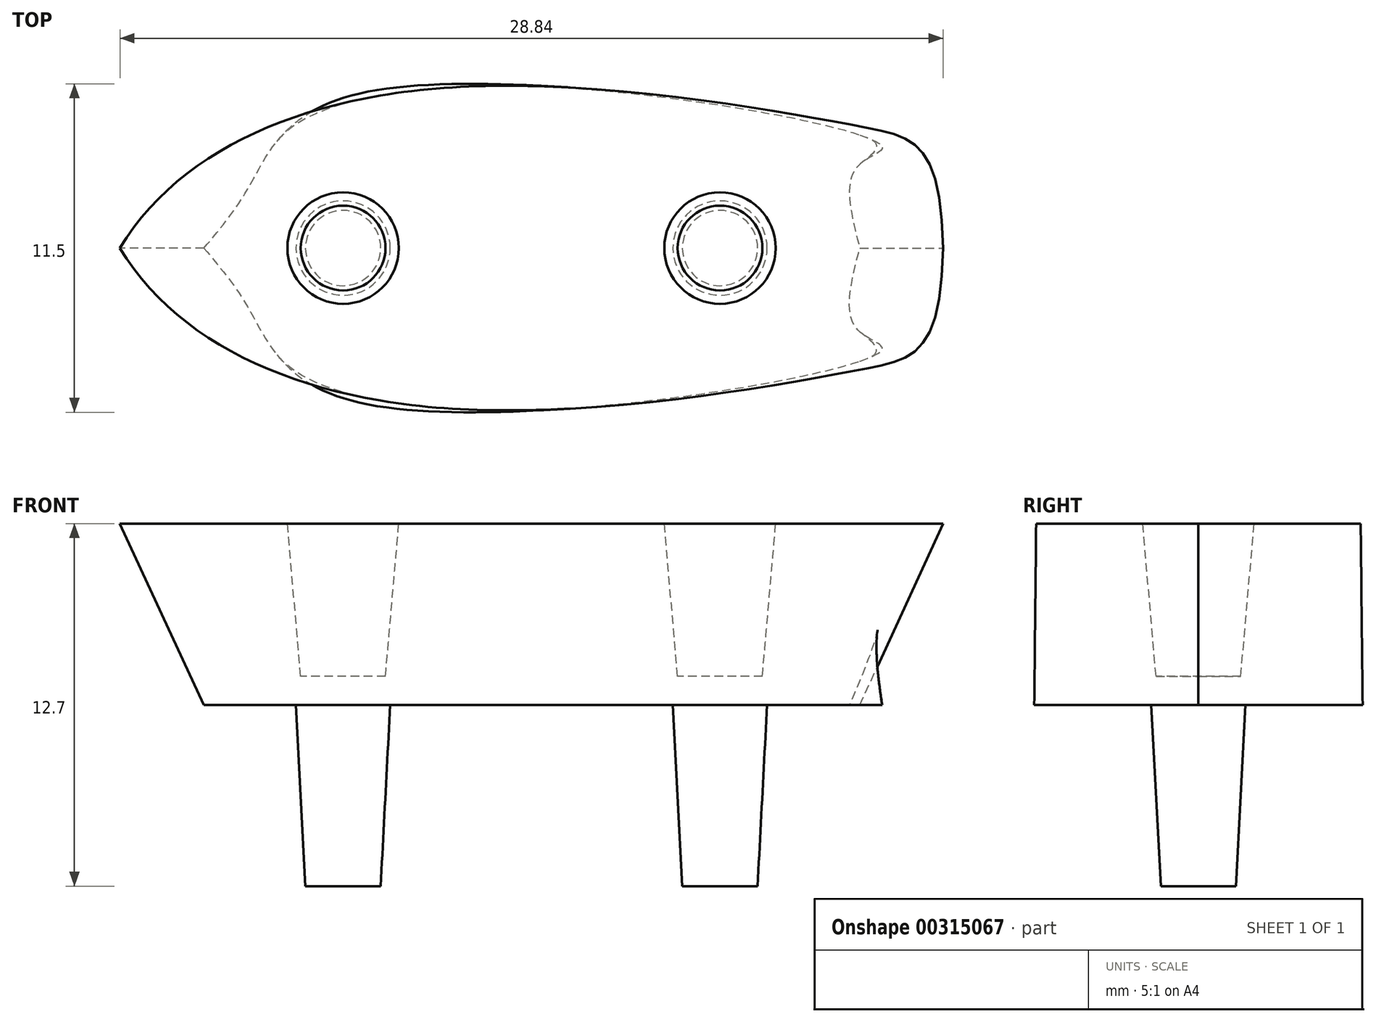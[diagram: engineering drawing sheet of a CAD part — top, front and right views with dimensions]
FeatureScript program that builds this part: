
annotation { "Feature Type Name" : "Feature", "Feature Type Description" : "" }
export const myFeature = defineFeature(function(context is Context, id is Id, definition is map)
    precondition{}
    {
        {
            var Q0;
            Q0=qCreatedBy(makeId("Top.planeOp"),FACE);
            var sketch = newSketch(context, id + "F0", { "sketchPlane" : qUnion([Q0])});
            skCircle(sketch, "E0", {"center": v(-6.6, 0) * mm, "radius": 1.65 * mm});
            skCircle(sketch, "E1", {"center": v(6.6, 0) * mm, "radius": 1.65 * mm});
            skFitSpline(sketch, "E2", {"points": [v(-14.42, 0) * mm, v(-3.67, 5.56) * mm, v(11.5, 4.26) * mm, v(14.42, 0) * mm], "startDerivative": vector(16.36, 27.23) * mm, "endDerivative": vector(1.16, -47.54) * mm});
            skFitSpline(sketch, "E3.MirrorCS", {"points": [v(-14.42, 0) * mm, v(-3.67, -5.56) * mm, v(11.5, -4.26) * mm, v(14.42, 0) * mm], "startDerivative": vector(16.36, -27.23) * mm, "endDerivative": vector(1.16, 47.54) * mm});
            skFitSpline(sketch, "E4", {"points": [v(-11.48, 0) * mm, v(-4.9, 4.04) * mm, v(10.6, 3.36) * mm, v(11.48, 0) * mm], "startDerivative": vector(14.55, 19.73) * mm, "endDerivative": vector(1.2, -39.33) * mm});
            skFitSpline(sketch, "E5.MirrorCS", {"points": [v(-11.48, 0) * mm, v(-4.9, -4.04) * mm, v(10.6, -3.36) * mm, v(11.48, 0) * mm], "startDerivative": vector(14.55, -19.73) * mm, "endDerivative": vector(1.2, 39.33) * mm});
            skCircle(sketch, "E6.0", {"center": v(-6.6, 0) * mm, "radius": 1.4 * mm});
            skCircle(sketch, "E7.0", {"center": v(6.6, 0) * mm, "radius": 1.4 * mm});
            skSolve(sketch);
        }
        {
            var Q0;
            Q0=qCreatedBy(makeId("Top.planeOp"),FACE);
            cPlane(context, id + "F1", {"entities" : qUnion([Q0]), "cplaneType" : CPlaneType.OFFSET, "offset" : 6.35 * mm, "width" : 152.4 * mm, "height" : 152.4 * mm});
        }
        {
            var Q0;
            Q0=qCreatedBy(id+"F1.planeOp",FACE);
            var sketch = newSketch(context, id + "F2", { "sketchPlane" : qUnion([Q0])});
            skFitSpline(sketch, "E8", {"points": [v(-14.42, 0) * mm, v(-3.67, 5.56) * mm, v(11.5, 4.26) * mm, v(14.42, 0) * mm], "startDerivative": vector(16.36, 27.23) * mm, "endDerivative": vector(1.16, -47.54) * mm});
            skFitSpline(sketch, "E9.MirrorCS", {"points": [v(-14.42, 0) * mm, v(-3.67, -5.56) * mm, v(11.5, -4.26) * mm, v(14.42, 0) * mm], "startDerivative": vector(16.36, -27.23) * mm, "endDerivative": vector(1.16, 47.54) * mm});
            skSolve(sketch);
        }
        {
            var Q0;
            Q0=qCreatedBy(makeId("Top.planeOp"),FACE);
            var sketch = newSketch(context, id + "F3", { "sketchPlane" : qUnion([Q0])});
            skFitSpline(sketch, "E10.0", {"points": [v(-11.48, 0) * mm, v(-9.9, 2.13) * mm, v(-6, 5.42) * mm, v(12.28, 3.56) * mm, v(11.42, 2.85) * mm, v(11.5, 0) * mm]});
            skFitSpline(sketch, "E10.1", {"points": [v(-11.48, 0) * mm, v(-9.9, -2.13) * mm, v(-6, -5.42) * mm, v(12.28, -3.56) * mm, v(11.42, -2.85) * mm, v(11.5, 0) * mm]});
            skSolve(sketch);
        }
        {
            var Q0;
            Q0 = qSketchRegion(id + "F3", true);
            var Q1;
            Q1 = qSketchRegion(id + "F2", true);
            loft(context, id + "F4", {"sheetProfilesArray" : [{ "sheetProfileEntities" : qUnion([Q0]) }, { "sheetProfileEntities" : qUnion([Q1]) }]});
        }
        {
            var Q0;
            Q0=makeQuery(id+"F0.imprint","IMPRINT",FACE,{"disambiguationData":[TD([[makeQuery(id+"F0.imprint","IMPRINT",EDGE,{"derivedFrom":sQuery(id+"F0.wireOp",EDGE,"E6.0")}),1.0]])]});
            var Q1;
            Q1=makeQuery(id+"F0.imprint","IMPRINT",FACE,{"disambiguationData":[TD([[makeQuery(id+"F0.imprint","IMPRINT",EDGE,{"derivedFrom":sQuery(id+"F0.wireOp",EDGE,"E7.0")}),1.0]])]});
            var Q2;
            Q2=sQuery(id+"F0.wireOp",EDGE,"E7.0");
            var Q3;
            Q3=sQuery(id+"F0.wireOp",EDGE,"E6.0");
            extrude(context, id + "F5", {"entities" : qUnion([Q0, Q1]), "operationType" : NewBodyOperationType.REMOVE, "surfaceEntities" : qUnion([Q2, Q3]), "endBound" : BoundingType.THROUGH_ALL, "depth" : 25.4 * mm, "hasDraft" : true, "draftAngle" : 5 * degree, "hasSecondDirection" : true, "secondDirectionOppositeDirection" : false, "secondDirectionDepth" : 1 * mm});
        }
        {
            var Q0;
            Q0=makeQuery(id+"F0.imprint","IMPRINT",FACE,{"disambiguationData":[TD([[makeQuery(id+"F0.imprint","IMPRINT",EDGE,{"derivedFrom":sQuery(id+"F0.wireOp",EDGE,"E0")}),1.0]])]});
            var Q1;
            Q1=makeQuery(id+"F0.imprint","IMPRINT",FACE,{"disambiguationData":[TD([[makeQuery(id+"F0.imprint","IMPRINT",EDGE,{"derivedFrom":sQuery(id+"F0.wireOp",EDGE,"E6.0")}),1.0]])]});
            var Q2;
            Q2=makeQuery(id+"F0.imprint","IMPRINT",FACE,{"disambiguationData":[TD([[makeQuery(id+"F0.imprint","IMPRINT",EDGE,{"derivedFrom":sQuery(id+"F0.wireOp",EDGE,"E1")}),1.0]])]});
            var Q3;
            Q3=makeQuery(id+"F0.imprint","IMPRINT",FACE,{"disambiguationData":[TD([[makeQuery(id+"F0.imprint","IMPRINT",EDGE,{"derivedFrom":sQuery(id+"F0.wireOp",EDGE,"E7.0")}),1.0]])]});
            extrude(context, id + "F6", {"entities" : qUnion([Q0, Q1, Q2, Q3]), "operationType" : NewBodyOperationType.ADD, "oppositeDirection" : true, "depth" : 6.35 * mm, "hasDraft" : true, "draftAngle" : 3 * degree, "draftPullDirection" : true});
        }
    });
